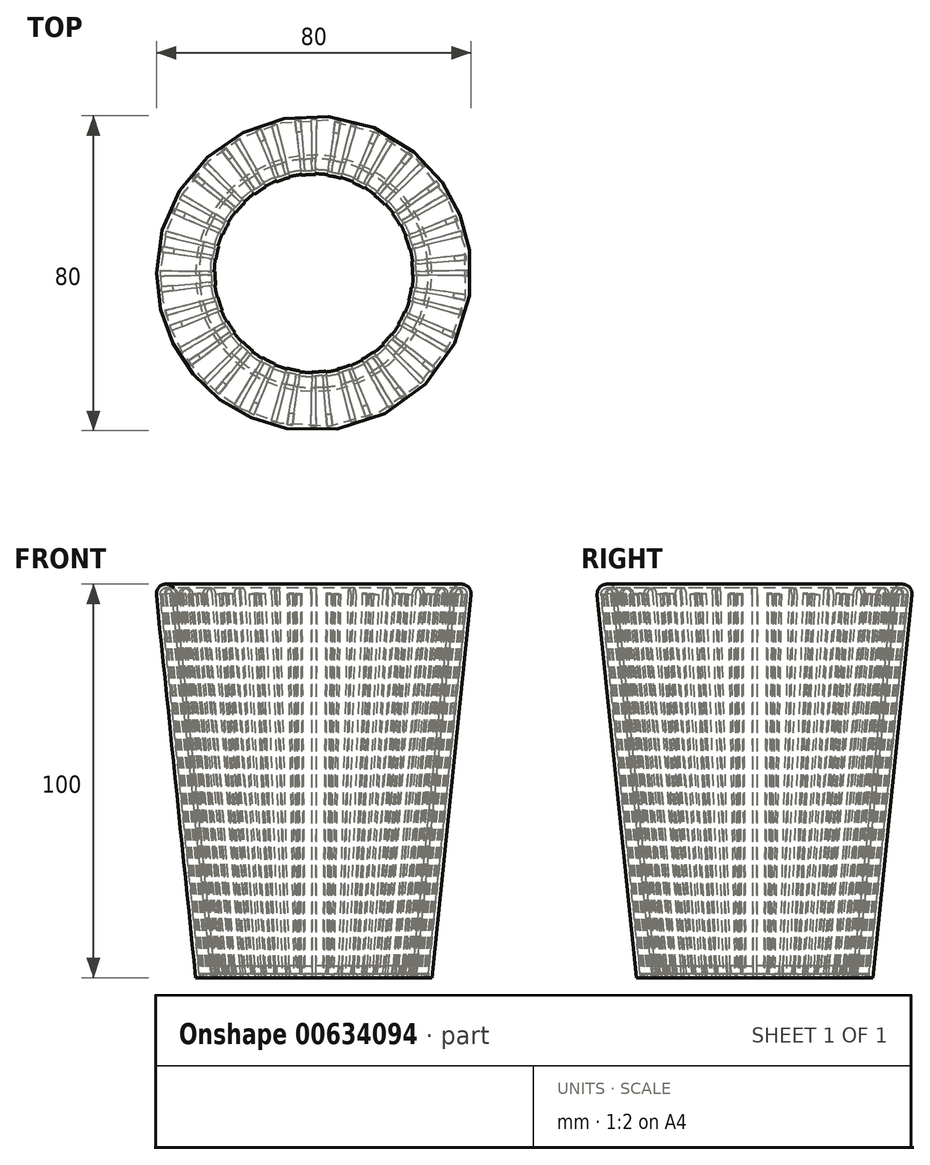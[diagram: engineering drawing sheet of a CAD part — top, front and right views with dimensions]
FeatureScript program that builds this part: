
annotation { "Feature Type Name" : "Feature", "Feature Type Description" : "" }
export const myFeature = defineFeature(function(context is Context, id is Id, definition is map)
    precondition{}
    {
        {
            var Q0;
            Q0=qCreatedBy(makeId("Front.planeOp"),FACE);
            var sketch = newSketch(context, id + "F0", { "sketchPlane" : qUnion([Q0])});
            skLineSegment(sketch, "E0.bottom", {"start": v(0, 0) * mm, "end": v(30, 0) * mm});
            skLineSegment(sketch, "E0.top", {"start": v(0, 1) * mm, "end": v(30, 1) * mm});
            skLineSegment(sketch, "E0.left", {"start": v(0, 0) * mm, "end": v(0, 1) * mm});
            skLineSegment(sketch, "E0.right", {"start": v(30, 0) * mm, "end": v(30, 1) * mm});
            skCircle(sketch, "E1", {"center": v(37.5, 97.5) * mm, "radius": 2.5 * mm});
            skLineSegment(sketch, "E2", {"start": v(39.99, 97.24) * mm, "end": v(30, 0) * mm});
            skLineSegment(sketch, "E3", {"start": v(35.01, 97.76) * mm, "end": v(25.08, 1) * mm});
            skCircle(sketch, "E4", {"center": v(37.5, 97.5) * mm, "radius": 1.5 * mm});
            skLineSegment(sketch, "E5", {"start": v(36, 97.65) * mm, "end": v(25.98, 0) * mm});
            skLineSegment(sketch, "E6", {"start": v(39, 97.35) * mm, "end": v(29, 0) * mm});
            skLineSegment(sketch, "E7.top", {"start": v(25.28, 3) * mm, "end": v(26.29, 3) * mm});
            skLineSegment(sketch, "E8", {"start": v(35.01, 97.76) * mm, "end": v(39.99, 97.24) * mm});
            skSolve(sketch);
        }
        {
            var Q0;
            {var subQ0=sQuery(id+"F0.wireOp",EDGE,"E5");var subQ1=sQuery(id+"F0.wireOp",EDGE,"E0.bottom");var subQ2=makeQuery(id+"F0.imprint","INTERSECT",VERTEX,{"derivedFrom":[subQ1,subQ0]});Q0=makeQuery(id+"F0.imprint","IMPRINT",FACE,{"disambiguationData":[TD([[makeQuery(id+"F0.imprint","IMPRINT",EDGE,{"disambiguationData":[TD([[subQ2,-1.0]])],"derivedFrom":subQ1}),1.0]])]});}
            var Q1;
            {var subQ5=sQuery(id+"F0.wireOp",EDGE,"E7.top");Q1=makeQuery(id+"F0.imprint","IMPRINT",FACE,{"disambiguationData":[TD([[makeQuery(id+"F0.imprint","IMPRINT",EDGE,{"derivedFrom":subQ5}),1.0]])]});}
            var Q2;
            {var subQ6=sQuery(id+"F0.wireOp",EDGE,"E0.right");Q2=makeQuery(id+"F0.imprint","IMPRINT",FACE,{"disambiguationData":[TD([[makeQuery(id+"F0.imprint","IMPRINT",EDGE,{"derivedFrom":subQ6}),-1.0]])]});}
            var Q3;
            {var subQ1=sQuery(id+"F0.wireOp",EDGE,"E1");var subQ3=sQuery(id+"F0.wireOp",EDGE,"E5");var subQ4=makeQuery(id+"F0.imprint","INTERSECT",VERTEX,{"derivedFrom":[subQ1,subQ3]});Q3=makeQuery(id+"F0.imprint","IMPRINT",FACE,{"disambiguationData":[TD([[makeQuery(id+"F0.imprint","IMPRINT",EDGE,{"disambiguationData":[TD([[subQ4,1.0]])],"derivedFrom":subQ1}),1.0]])]});}
            var Q4;
            {var subQ1=sQuery(id+"F0.wireOp",EDGE,"E1");var subQ3=sQuery(id+"F0.wireOp",EDGE,"E6");var subQ4=makeQuery(id+"F0.imprint","INTERSECT",VERTEX,{"derivedFrom":[subQ1,subQ3]});Q4=makeQuery(id+"F0.imprint","IMPRINT",FACE,{"disambiguationData":[TD([[makeQuery(id+"F0.imprint","IMPRINT",EDGE,{"disambiguationData":[TD([[subQ4,-1.0]])],"derivedFrom":subQ1}),1.0]])]});}
            var Q5;
            {var subQ0=sQuery(id+"F0.wireOp",EDGE,"E0.left");Q5=makeQuery(id+"F0.imprint","IMPRINT",FACE,{"disambiguationData":[TD([[makeQuery(id+"F0.imprint","IMPRINT",EDGE,{"derivedFrom":subQ0}),-1.0]])]});}
            var Q6;
            {var subQ5=sQuery(id+"F0.wireOp",EDGE,"E7.top");Q6=makeQuery(id+"F0.imprint","IMPRINT",FACE,{"disambiguationData":[TD([[makeQuery(id+"F0.imprint","IMPRINT",EDGE,{"derivedFrom":subQ5}),-1.0]])]});}
            var Q7;
            {var subQ0=sQuery(id+"F0.wireOp",EDGE,"E0.right");Q7=makeQuery(id+"F0.imprint","IMPRINT",FACE,{"disambiguationData":[TD([[makeQuery(id+"F0.imprint","IMPRINT",EDGE,{"derivedFrom":subQ0}),1.0]])]});}
            var Q8;
            {var subQ0=sQuery(id+"F0.wireOp",EDGE,"E8");var subQ1=sQuery(id+"F0.wireOp",EDGE,"E1");var subQ2=makeQuery(id+"F0.imprint","INTERSECT",VERTEX,{"derivedFrom":[subQ1,sQuery(id+"F0.wireOp",EDGE,"E2"),subQ0]});Q8=makeQuery(id+"F0.imprint","IMPRINT",FACE,{"disambiguationData":[TD([[makeQuery(id+"F0.imprint","IMPRINT",EDGE,{"disambiguationData":[TD([[subQ2,-1.0]])],"derivedFrom":subQ1}),1.0]])]});}
            var Q9;
            Q9=sQuery(id+"F0.wireOp",EDGE,"E0.left");
            revolve(context, id + "F1", {"entities" : qUnion([Q0, Q1, Q2, Q3, Q4, Q5, Q6, Q7, Q8]), "axis" : qUnion([Q9]), "revolveType" : RevolveType.FULL});
        }
        {
            var Q0;
            {var subQ0=sQuery(id+"F0.wireOp",EDGE,"E8");var subQ1=sQuery(id+"F0.wireOp",EDGE,"E4");var subQ2=makeQuery(id+"F0.imprint","INTERSECT",VERTEX,{"derivedFrom":[subQ1,sQuery(id+"F0.wireOp",EDGE,"E5"),subQ0]});Q0=makeQuery(id+"F0.imprint","IMPRINT",FACE,{"disambiguationData":[TD([[makeQuery(id+"F0.imprint","IMPRINT",EDGE,{"disambiguationData":[TD([[subQ2,1.0]])],"derivedFrom":subQ1}),1.0]])]});}
            var Q1;
            {var subQ0=sQuery(id+"F0.wireOp",EDGE,"E8");var subQ1=sQuery(id+"F0.wireOp",EDGE,"E4");var subQ2=makeQuery(id+"F0.imprint","INTERSECT",VERTEX,{"derivedFrom":[subQ1,sQuery(id+"F0.wireOp",EDGE,"E5"),subQ0]});Q1=makeQuery(id+"F0.imprint","IMPRINT",FACE,{"disambiguationData":[TD([[makeQuery(id+"F0.imprint","IMPRINT",EDGE,{"disambiguationData":[TD([[subQ2,-1.0]])],"derivedFrom":subQ1}),1.0]])]});}
            var Q2;
            {var subQ0=sQuery(id+"F0.wireOp",EDGE,"E5");var subQ1=sQuery(id+"F0.wireOp",EDGE,"E1");var subQ2=makeQuery(id+"F0.imprint","INTERSECT",VERTEX,{"derivedFrom":[subQ1,subQ0]});Q2=makeQuery(id+"F0.imprint","IMPRINT",FACE,{"disambiguationData":[TD([[makeQuery(id+"F0.imprint","IMPRINT",EDGE,{"disambiguationData":[TD([[subQ2,-1.0]])],"derivedFrom":subQ1}),1.0]])]});}
            var Q3;
            {var subQ0=sQuery(id+"F0.wireOp",EDGE,"E5");var subQ4=sQuery(id+"F0.wireOp",EDGE,"E0.top");var subQ5=makeQuery(id+"F0.imprint","INTERSECT",VERTEX,{"derivedFrom":[subQ4,subQ0]});Q3=makeQuery(id+"F0.imprint","IMPRINT",FACE,{"disambiguationData":[TD([[makeQuery(id+"F0.imprint","IMPRINT",EDGE,{"disambiguationData":[TD([[subQ5,-1.0]])],"derivedFrom":subQ4}),1.0]])]});}
            var Q4;
            Q4=sQuery(id+"F0.wireOp",EDGE,"E0.left");
            revolve(context, id + "F2", {"entities" : qUnion([Q0, Q1, Q2, Q3]), "axis" : qUnion([Q4]), "revolveType" : RevolveType.SYMMETRIC, "angle" : 2 * degree});
        }
        {
            var Q0;
            Q0=makeQuery(id+"F2.opRevolve","SWEPT_BODY",BODY,{"disambiguationData":[OSD([sQuery(id+"F0.wireOp",EDGE,"E0.top"),sQuery(id+"F0.wireOp",EDGE,"E4"),sQuery(id+"F0.wireOp",EDGE,"E5"),sQuery(id+"F0.wireOp",EDGE,"E6")])]});
            var Q1;
            Q1=sQuery(id+"F0.wireOp",EDGE,"E0.left");
            circularPattern(context, id + "F3", {"entities" : qUnion([Q0]), "axis" : qUnion([Q1]), "angle" : 360 * degree, "instanceCount" : 24, "equalSpace" : true});
        }
        {
            var Q0;
            {var subQ0=sQuery(id+"F0.wireOp",EDGE,"E8");var subQ1=sQuery(id+"F0.wireOp",EDGE,"E4");var subQ2=makeQuery(id+"F0.imprint","INTERSECT",VERTEX,{"derivedFrom":[subQ1,sQuery(id+"F0.wireOp",EDGE,"E5"),subQ0]});Q0=makeQuery(id+"F0.imprint","IMPRINT",FACE,{"disambiguationData":[TD([[makeQuery(id+"F0.imprint","IMPRINT",EDGE,{"disambiguationData":[TD([[subQ2,-1.0]])],"derivedFrom":subQ1}),1.0]])]});}
            var Q1;
            {var subQ0=sQuery(id+"F0.wireOp",EDGE,"E5");var subQ1=sQuery(id+"F0.wireOp",EDGE,"E1");var subQ2=makeQuery(id+"F0.imprint","INTERSECT",VERTEX,{"derivedFrom":[subQ1,subQ0]});Q1=makeQuery(id+"F0.imprint","IMPRINT",FACE,{"disambiguationData":[TD([[makeQuery(id+"F0.imprint","IMPRINT",EDGE,{"disambiguationData":[TD([[subQ2,-1.0]])],"derivedFrom":subQ1}),1.0]])]});}
            var Q2;
            {var subQ0=sQuery(id+"F0.wireOp",EDGE,"E5");var subQ4=sQuery(id+"F0.wireOp",EDGE,"E0.top");var subQ5=makeQuery(id+"F0.imprint","INTERSECT",VERTEX,{"derivedFrom":[subQ4,subQ0]});Q2=makeQuery(id+"F0.imprint","IMPRINT",FACE,{"disambiguationData":[TD([[makeQuery(id+"F0.imprint","IMPRINT",EDGE,{"disambiguationData":[TD([[subQ5,-1.0]])],"derivedFrom":subQ4}),1.0]])]});}
            var Q3;
            Q3=sQuery(id+"F0.wireOp",EDGE,"E0.left");
            revolve(context, id + "F4", {"entities" : qUnion([Q0, Q1, Q2]), "axis" : qUnion([Q3]), "revolveType" : RevolveType.SYMMETRIC, "angle" : 2 * degree});
        }
        {
            var Q0;
            Q0=makeQuery(id+"F4.opRevolve","SWEPT_BODY",BODY,{"disambiguationData":[OSD([sQuery(id+"F0.wireOp",EDGE,"E0.top"),sQuery(id+"F0.wireOp",EDGE,"E5"),sQuery(id+"F0.wireOp",EDGE,"E6"),sQuery(id+"F0.wireOp",EDGE,"E8")])]});
            var Q1;
            Q1=sQuery(id+"F0.wireOp",EDGE,"E0.left");
            transform(context, id + "F5", {"entities" : qUnion([Q0]), "transformType" : TransformType.ROTATION, "transformAxis" : qUnion([Q1]), "angle" : 6 * degree, "makeCopy" : false});
        }
        {
            var Q0;
            Q0=makeQuery(id+"F4.opRevolve","SWEPT_BODY",BODY,{"disambiguationData":[OSD([sQuery(id+"F0.wireOp",EDGE,"E0.top"),sQuery(id+"F0.wireOp",EDGE,"E5"),sQuery(id+"F0.wireOp",EDGE,"E6"),sQuery(id+"F0.wireOp",EDGE,"E8")])]});
            var Q1;
            Q1=sQuery(id+"F0.wireOp",EDGE,"E0.left");
            circularPattern(context, id + "F6", {"entities" : qUnion([Q0]), "axis" : qUnion([Q1]), "angle" : 360 * degree, "instanceCount" : 24, "equalSpace" : true});
        }
        {
            var Q0;
            {var subQ0=sQuery(id+"F0.wireOp",EDGE,"E5");var subQ1=sQuery(id+"F0.wireOp",EDGE,"E0.bottom");var subQ2=makeQuery(id+"F0.imprint","INTERSECT",VERTEX,{"derivedFrom":[subQ1,subQ0]});Q0=makeQuery(id+"F0.imprint","IMPRINT",FACE,{"disambiguationData":[TD([[makeQuery(id+"F0.imprint","IMPRINT",EDGE,{"disambiguationData":[TD([[subQ2,-1.0]])],"derivedFrom":subQ1}),1.0]])]});}
            var Q1;
            Q1=sQuery(id+"F0.wireOp",EDGE,"E0.left");
            revolve(context, id + "F7", {"entities" : qUnion([Q0]), "axis" : qUnion([Q1]), "revolveType" : RevolveType.TWO_DIRECTIONS, "angle" : 5 * degree, "angleBack" : 1 * degree});
        }
        {
            var Q0;
            Q0=makeQuery(id+"F7.opRevolve","SWEPT_BODY",BODY,{"disambiguationData":[OSD([sQuery(id+"F0.wireOp",EDGE,"E0.bottom"),sQuery(id+"F0.wireOp",EDGE,"E0.top"),sQuery(id+"F0.wireOp",EDGE,"E5"),sQuery(id+"F0.wireOp",EDGE,"E6")])]});
            var Q1;
            Q1=sQuery(id+"F0.wireOp",EDGE,"E0.left");
            circularPattern(context, id + "F8", {"operationType" : NewBodyOperationType.REMOVE, "entities" : qUnion([Q0]), "axis" : qUnion([Q1]), "angle" : 360 * degree, "instanceCount" : 24, "equalSpace" : true});
        }
        {
            var Q0;
            {var subQ5=sQuery(id+"F0.wireOp",EDGE,"E7.top");Q0=makeQuery(id+"F0.imprint","IMPRINT",FACE,{"disambiguationData":[TD([[makeQuery(id+"F0.imprint","IMPRINT",EDGE,{"derivedFrom":subQ5}),-1.0]])]});}
            var Q1;
            Q1=sQuery(id+"F0.wireOp",EDGE,"E0.left");
            revolve(context, id + "F9", {"entities" : qUnion([Q0]), "axis" : qUnion([Q1]), "revolveType" : RevolveType.TWO_DIRECTIONS, "oppositeDirection" : true, "angle" : 8 * degree, "angleBack" : 1 * degree});
        }
        {
            var Q0;
            Q0=makeQuery(id+"F9.opRevolve","SWEPT_BODY",BODY,{"disambiguationData":[OSD([sQuery(id+"F0.wireOp",EDGE,"E0.top"),sQuery(id+"F0.wireOp",EDGE,"E3"),sQuery(id+"F0.wireOp",EDGE,"E5"),sQuery(id+"F0.wireOp",EDGE,"E7.top")])]});
            var Q1;
            Q1=sQuery(id+"F0.wireOp",EDGE,"E0.left");
            circularPattern(context, id + "F10", {"operationType" : NewBodyOperationType.REMOVE, "entities" : qUnion([Q0]), "axis" : qUnion([Q1]), "angle" : 360 * degree, "instanceCount" : 24, "equalSpace" : true});
        }
    });
